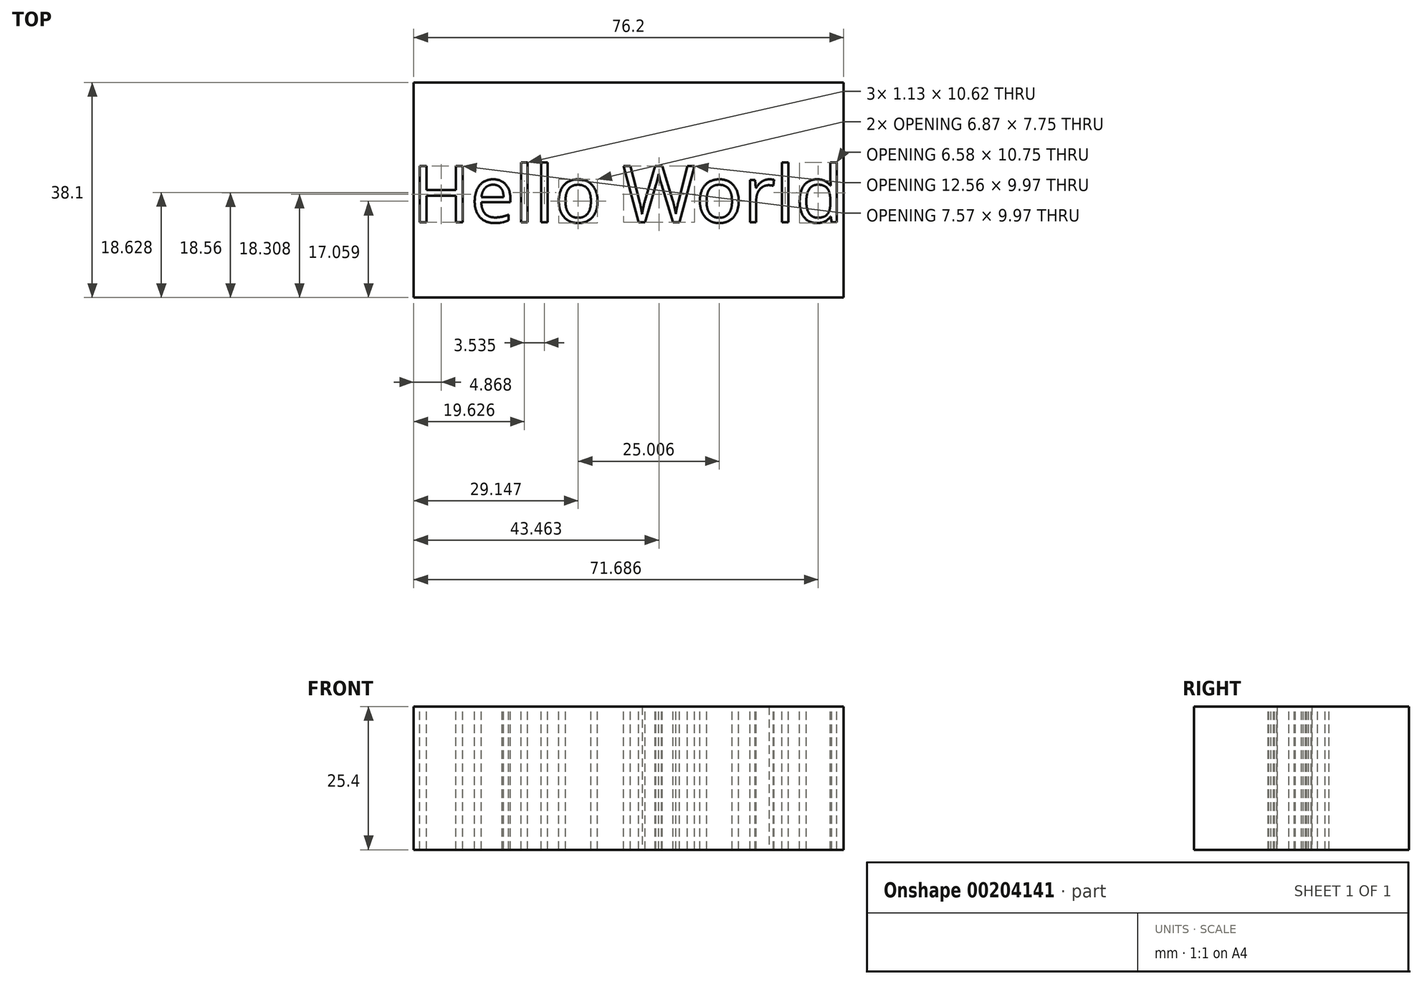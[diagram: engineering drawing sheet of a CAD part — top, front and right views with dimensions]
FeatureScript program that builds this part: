
annotation { "Feature Type Name" : "Feature", "Feature Type Description" : "" }
export const myFeature = defineFeature(function(context is Context, id is Id, definition is map)
    precondition{}
    {
        {
            var Q0;
            Q0=qCreatedBy(makeId("Front.planeOp"),FACE);
            var sketch = newSketch(context, id + "F0", { "sketchPlane" : qUnion([Q0])});
            skLineSegment(sketch, "E0.bottom", {"start": v(0, 0) * mm, "end": v(76.2, 0) * mm});
            skLineSegment(sketch, "E0.top", {"start": v(0, 25.4) * mm, "end": v(76.2, 25.4) * mm});
            skLineSegment(sketch, "E0.left", {"start": v(0, 0) * mm, "end": v(0, 25.4) * mm});
            skLineSegment(sketch, "E0.right", {"start": v(76.2, 0) * mm, "end": v(76.2, 25.4) * mm});
            skSolve(sketch);
        }
        {
            var Q0;
            Q0=makeQuery(id+"F0.imprint","IMPRINT",FACE,{"disambiguationData":[TD([[makeQuery(id+"F0.imprint","IMPRINT",EDGE,{"derivedFrom":sQuery(id+"F0.wireOp",EDGE,"E0.bottom")}),1.0]])]});
            extrude(context, id + "F1", {"entities" : qUnion([Q0]), "depth" : 38.1 * mm});
        }
        {
            var Q0;
            Q0=makeQuery(id+"F1.opExtrude","SWEPT_FACE",FACE,{"disambiguationData":[OSD([sQuery(id+"F0.wireOp",EDGE,"E0.top")])]});
            var sketch = newSketch(context, id + "F2", { "sketchPlane" : qUnion([Q0])});
            skText(sketch, "E1", { "text": "Hello World", "fontName": "OpenSans-Regular.ttf"});
            const initialGuessF2  = {"E1": [-0.00029, -0.02478, 1, 0, 0.01006]};
            skSetInitialGuess(sketch, initialGuessF2);
            skSolve(sketch);
        }
        {
            var Q0;
            Q0 = qSketchRegion(id + "F2", true);
            extrude(context, id + "F3", {"entities" : qUnion([Q0]), "operationType" : NewBodyOperationType.REMOVE, "oppositeDirection" : true, "depth" : 25.4 * mm});
        }
    });
